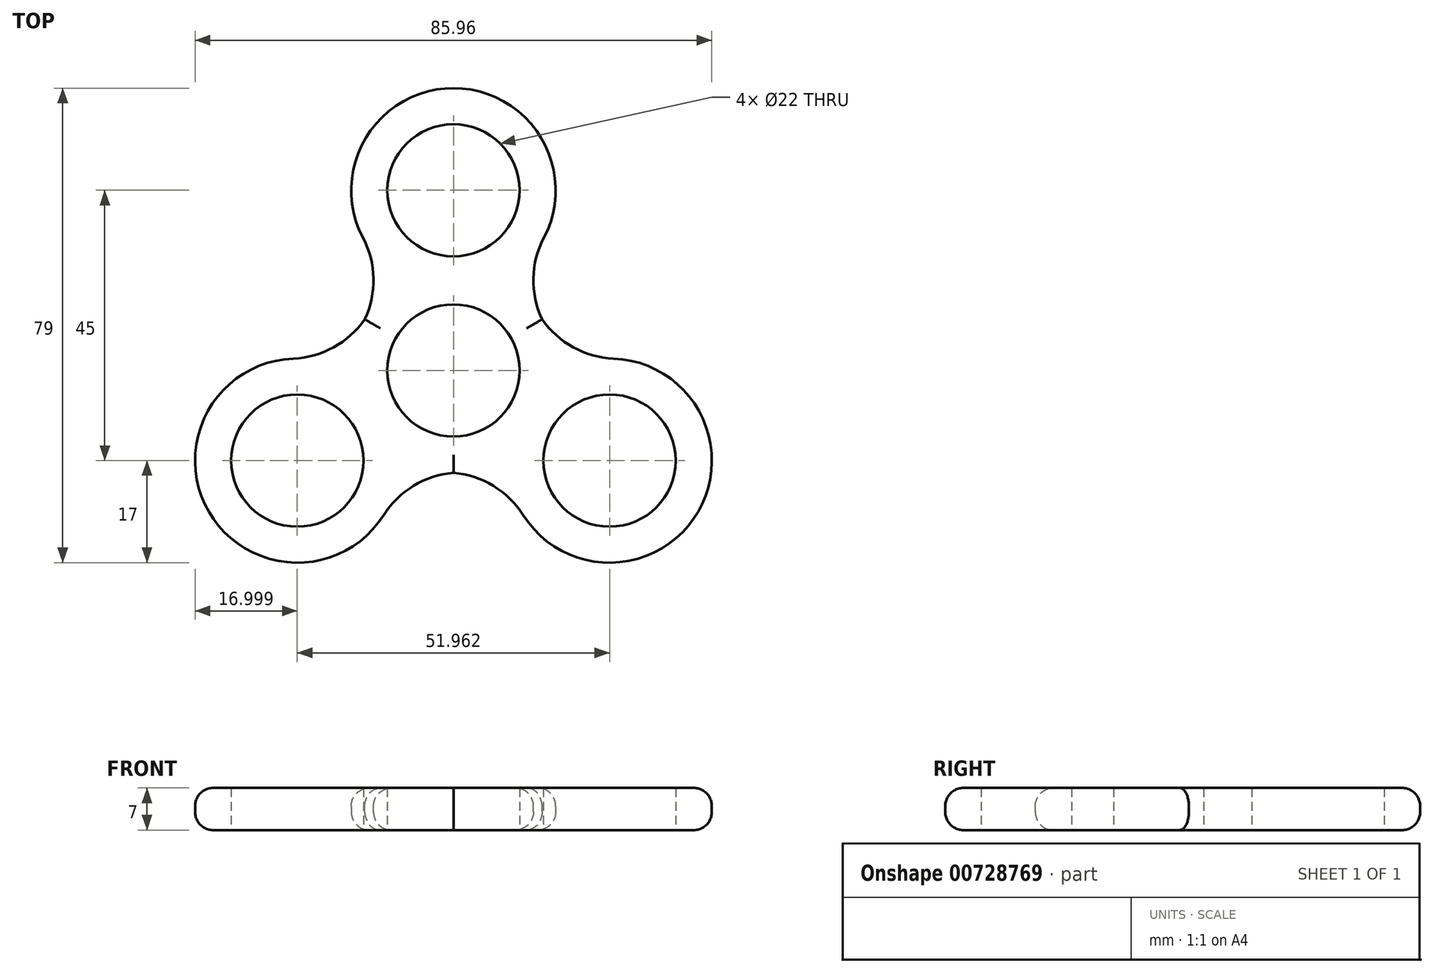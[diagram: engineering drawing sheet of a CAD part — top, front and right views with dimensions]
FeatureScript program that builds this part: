
annotation { "Feature Type Name" : "Feature", "Feature Type Description" : "" }
export const myFeature = defineFeature(function(context is Context, id is Id, definition is map)
    precondition{}
    {
        {
            var Q0;
            Q0=qCreatedBy(makeId("Top.planeOp"),FACE);
            var sketch = newSketch(context, id + "F0", { "sketchPlane" : qUnion([Q0])});
            skCircle(sketch, "E0", {"center": v(0, 0) * mm, "radius": 11 * mm});
            skCircle(sketch, "E1.0", {"center": v(0, 0) * mm, "radius": 17 * mm});
            skLineSegment(sketch, "E2", {"start": v(-11, 0) * mm, "end": v(0, 0) * mm});
            skLineSegment(sketch, "E3", {"start": v(0, 0) * mm, "end": v(0, 30) * mm});
            skCircle(sketch, "E4", {"center": v(0, 30) * mm, "radius": 11 * mm});
            skCircle(sketch, "E5.0", {"center": v(0, 30) * mm, "radius": 17 * mm});
            skCircle(sketch, "E6.1.1", {"center": v(-25.98, -15) * mm, "radius": 11 * mm});
            skCircle(sketch, "E6.1.2", {"center": v(-25.98, -15) * mm, "radius": 17 * mm});
            skCircle(sketch, "E6.2.1", {"center": v(25.98, -15) * mm, "radius": 11 * mm});
            skCircle(sketch, "E6.2.2", {"center": v(25.98, -15) * mm, "radius": 17 * mm});
            skLineSegment(sketch, "E7", {"start": v(-25.98, -15) * mm, "end": v(-25.98, 2) * mm});
            skLineSegment(sketch, "E8", {"start": v(0, 0) * mm, "end": v(0, -17) * mm});
            skSolve(sketch);
        }
        {
            var Q0;
            Q0=makeQuery(id+"F0.imprint","IMPRINT",FACE,{"disambiguationData":[TD([[makeQuery(id+"F0.imprint","IMPRINT",EDGE,{"derivedFrom":sQuery(id+"F0.wireOp",EDGE,"E4")}),-1.0]])]});
            var Q1;
            {var subQ0=sQuery(id+"F0.wireOp",EDGE,"E5.0");var subQ1=sQuery(id+"F0.wireOp",EDGE,"E1.0");var subQ2=makeQuery(id+"F0.imprint","INTERSECT",VERTEX,{"disambiguationData":[OD(1.0)],"derivedFrom":[subQ1,subQ0]});Q1=makeQuery(id+"F0.imprint","IMPRINT",FACE,{"disambiguationData":[TD([[makeQuery(id+"F0.imprint","IMPRINT",EDGE,{"disambiguationData":[TD([[subQ2,-1.0]])],"derivedFrom":subQ1}),1.0]])]});}
            var Q2;
            {var subQ1=sQuery(id+"F0.wireOp",EDGE,"E1.0");var subQ9=sQuery(id+"F0.wireOp",EDGE,"E8");var subQ10=makeQuery(id+"F0.imprint","INTERSECT",VERTEX,{"derivedFrom":[subQ1,subQ9]});Q2=makeQuery(id+"F0.imprint","IMPRINT",FACE,{"disambiguationData":[TD([[makeQuery(id+"F0.imprint","IMPRINT",EDGE,{"disambiguationData":[TD([[subQ10,-1.0]])],"derivedFrom":subQ1}),1.0]])]});}
            var Q3;
            {var subQ0=sQuery(id+"F0.wireOp",EDGE,"E6.2.2");var subQ1=sQuery(id+"F0.wireOp",EDGE,"E1.0");var subQ2=makeQuery(id+"F0.imprint","INTERSECT",VERTEX,{"disambiguationData":[OD(0.0)],"derivedFrom":[subQ1,subQ0]});Q3=makeQuery(id+"F0.imprint","IMPRINT",FACE,{"disambiguationData":[TD([[makeQuery(id+"F0.imprint","IMPRINT",EDGE,{"disambiguationData":[TD([[subQ2,-1.0]])],"derivedFrom":subQ1}),1.0]])]});}
            var Q4;
            {var subQ0=sQuery(id+"F0.wireOp",EDGE,"E6.1.2");var subQ1=sQuery(id+"F0.wireOp",EDGE,"E1.0");var subQ2=makeQuery(id+"F0.imprint","INTERSECT",VERTEX,{"disambiguationData":[OD(0.0)],"derivedFrom":[subQ1,subQ0]});Q4=makeQuery(id+"F0.imprint","IMPRINT",FACE,{"disambiguationData":[TD([[makeQuery(id+"F0.imprint","IMPRINT",EDGE,{"disambiguationData":[TD([[subQ2,-1.0]])],"derivedFrom":subQ1}),1.0]])]});}
            var Q5;
            Q5=makeQuery(id+"F0.imprint","IMPRINT",FACE,{"disambiguationData":[TD([[makeQuery(id+"F0.imprint","IMPRINT",EDGE,{"derivedFrom":sQuery(id+"F0.wireOp",EDGE,"E6.1.1")}),-1.0]])]});
            var Q6;
            {var subQ0=sQuery(id+"F0.wireOp",EDGE,"E3");var subQ1=sQuery(id+"F0.wireOp",EDGE,"E1.0");var subQ2=makeQuery(id+"F0.imprint","INTERSECT",VERTEX,{"derivedFrom":[subQ1,subQ0]});Q6=makeQuery(id+"F0.imprint","IMPRINT",FACE,{"disambiguationData":[TD([[makeQuery(id+"F0.imprint","IMPRINT",EDGE,{"disambiguationData":[TD([[subQ2,-1.0]])],"derivedFrom":subQ1}),1.0]])]});}
            var Q7;
            {var subQ0=sQuery(id+"F0.wireOp",EDGE,"E3");var subQ1=sQuery(id+"F0.wireOp",EDGE,"E1.0");var subQ2=makeQuery(id+"F0.imprint","INTERSECT",VERTEX,{"derivedFrom":[subQ1,subQ0]});Q7=makeQuery(id+"F0.imprint","IMPRINT",FACE,{"disambiguationData":[TD([[makeQuery(id+"F0.imprint","IMPRINT",EDGE,{"disambiguationData":[TD([[subQ2,1.0]])],"derivedFrom":subQ1}),1.0]])]});}
            var Q8;
            Q8=makeQuery(id+"F0.imprint","IMPRINT",FACE,{"disambiguationData":[TD([[makeQuery(id+"F0.imprint","IMPRINT",EDGE,{"derivedFrom":sQuery(id+"F0.wireOp",EDGE,"E6.2.1")}),-1.0]])]});
            extrude(context, id + "F1", {"entities" : qUnion([Q0, Q1, Q2, Q3, Q4, Q5, Q6, Q7, Q8]), "depth" : 7 * mm, "offsetDistance" : 25.4 * mm});
        }
        {
            var Q0;
            {var subQ0=sQuery(id+"F0.wireOp",EDGE,"E6.1.2");var subQ1=sQuery(id+"F0.wireOp",EDGE,"E1.0");Q0=makeQuery(id+"F1.opExtrude","SWEPT_EDGE",EDGE,{"disambiguationData":[OSD([subQ1,subQ0]),TDD([makeQuery(id+"F0.imprint","INTERSECT",VERTEX,{"disambiguationData":[OD(0.0)],"derivedFrom":[subQ1,subQ0]})])]});}
            var Q1;
            {var subQ0=sQuery(id+"F0.wireOp",EDGE,"E5.0");var subQ1=sQuery(id+"F0.wireOp",EDGE,"E1.0");Q1=makeQuery(id+"F1.opExtrude","SWEPT_EDGE",EDGE,{"disambiguationData":[OSD([subQ1,subQ0]),TDD([makeQuery(id+"F0.imprint","INTERSECT",VERTEX,{"disambiguationData":[OD(1.0)],"derivedFrom":[subQ1,subQ0]})])]});}
            var Q2;
            {var subQ0=sQuery(id+"F0.wireOp",EDGE,"E6.2.2");var subQ1=sQuery(id+"F0.wireOp",EDGE,"E1.0");Q2=makeQuery(id+"F1.opExtrude","SWEPT_EDGE",EDGE,{"disambiguationData":[OSD([subQ1,subQ0]),TDD([makeQuery(id+"F0.imprint","INTERSECT",VERTEX,{"disambiguationData":[OD(0.0)],"derivedFrom":[subQ1,subQ0]})])]});}
            var Q3;
            {var subQ0=sQuery(id+"F0.wireOp",EDGE,"E6.1.2");var subQ1=sQuery(id+"F0.wireOp",EDGE,"E1.0");Q3=makeQuery(id+"F1.opExtrude","SWEPT_EDGE",EDGE,{"disambiguationData":[OSD([subQ1,subQ0]),TDD([makeQuery(id+"F0.imprint","INTERSECT",VERTEX,{"disambiguationData":[OD(1.0)],"derivedFrom":[subQ1,subQ0]})])]});}
            var Q4;
            {var subQ0=sQuery(id+"F0.wireOp",EDGE,"E5.0");var subQ1=sQuery(id+"F0.wireOp",EDGE,"E1.0");Q4=makeQuery(id+"F1.opExtrude","SWEPT_EDGE",EDGE,{"disambiguationData":[OSD([subQ1,subQ0]),TDD([makeQuery(id+"F0.imprint","INTERSECT",VERTEX,{"disambiguationData":[OD(0.0)],"derivedFrom":[subQ1,subQ0]})])]});}
            var Q5;
            {var subQ0=sQuery(id+"F0.wireOp",EDGE,"E6.2.2");var subQ1=sQuery(id+"F0.wireOp",EDGE,"E1.0");Q5=makeQuery(id+"F1.opExtrude","SWEPT_EDGE",EDGE,{"disambiguationData":[OSD([subQ1,subQ0]),TDD([makeQuery(id+"F0.imprint","INTERSECT",VERTEX,{"disambiguationData":[OD(1.0)],"derivedFrom":[subQ1,subQ0]})])]});}
            fillet(context, id + "F2", {"entities" : qUnion([Q0, Q1, Q2, Q3, Q4, Q5]), "radius" : 15.24 * mm, "allowEdgeOverflow" : false});
        }
        {
            var Q0;
            Q0=makeQuery(id+"F1.opExtrude","CAP_EDGE",EDGE,{"disambiguationData":[OSD([sQuery(id+"F0.wireOp",EDGE,"E5.0")])],"isStart":false});
            var Q1;
            {var subQ0=sQuery(id+"F0.wireOp",EDGE,"E6.1.2");var subQ1=sQuery(id+"F0.wireOp",EDGE,"E1.0");Q1=makeQuery(id+"F2.opFillet","BLEND_EDGE",EDGE,{"blendedFrom":[makeQuery(id+"F1.opExtrude","SWEPT_EDGE",EDGE,{"disambiguationData":[OSD([subQ1,subQ0]),TDD([makeQuery(id+"F0.imprint","INTERSECT",VERTEX,{"disambiguationData":[OD(0.0)],"derivedFrom":[subQ1,subQ0]})])]}),makeQuery(id+"F1.opExtrude","CAP_FACE",FACE,{"disambiguationData":[OSD([subQ1,sQuery(id+"F0.wireOp",EDGE,"E4"),sQuery(id+"F0.wireOp",EDGE,"E5.0"),sQuery(id+"F0.wireOp",EDGE,"E6.1.1"),subQ0,sQuery(id+"F0.wireOp",EDGE,"E0"),sQuery(id+"F0.wireOp",EDGE,"E6.2.1"),sQuery(id+"F0.wireOp",EDGE,"E6.2.2")])],"isStart":false})],"blendedInto":[makeQuery(id+"F1.opExtrude","CAP_FACE",FACE,{"disambiguationData":[OSD([subQ1,sQuery(id+"F0.wireOp",EDGE,"E4"),sQuery(id+"F0.wireOp",EDGE,"E5.0"),sQuery(id+"F0.wireOp",EDGE,"E6.1.1"),subQ0,sQuery(id+"F0.wireOp",EDGE,"E0"),sQuery(id+"F0.wireOp",EDGE,"E6.2.1"),sQuery(id+"F0.wireOp",EDGE,"E6.2.2")])],"isStart":false})]});}
            var Q2;
            Q2=makeQuery(id+"F1.opExtrude","CAP_EDGE",EDGE,{"disambiguationData":[OSD([sQuery(id+"F0.wireOp",EDGE,"E6.1.2")])],"isStart":false});
            var Q3;
            Q3=makeQuery(id+"F1.opExtrude","CAP_EDGE",EDGE,{"disambiguationData":[OSD([sQuery(id+"F0.wireOp",EDGE,"E6.2.2")])],"isStart":false});
            var Q4;
            {var subQ0=sQuery(id+"F0.wireOp",EDGE,"E6.2.2");var subQ1=sQuery(id+"F0.wireOp",EDGE,"E1.0");Q4=makeQuery(id+"F2.opFillet","BLEND_EDGE",EDGE,{"blendedFrom":[makeQuery(id+"F1.opExtrude","SWEPT_EDGE",EDGE,{"disambiguationData":[OSD([subQ1,subQ0]),TDD([makeQuery(id+"F0.imprint","INTERSECT",VERTEX,{"disambiguationData":[OD(0.0)],"derivedFrom":[subQ1,subQ0]})])]}),makeQuery(id+"F1.opExtrude","CAP_FACE",FACE,{"disambiguationData":[OSD([subQ1,sQuery(id+"F0.wireOp",EDGE,"E4"),sQuery(id+"F0.wireOp",EDGE,"E5.0"),sQuery(id+"F0.wireOp",EDGE,"E6.1.1"),sQuery(id+"F0.wireOp",EDGE,"E6.1.2"),sQuery(id+"F0.wireOp",EDGE,"E0"),sQuery(id+"F0.wireOp",EDGE,"E6.2.1"),subQ0])],"isStart":false})],"blendedInto":[makeQuery(id+"F1.opExtrude","CAP_FACE",FACE,{"disambiguationData":[OSD([subQ1,sQuery(id+"F0.wireOp",EDGE,"E4"),sQuery(id+"F0.wireOp",EDGE,"E5.0"),sQuery(id+"F0.wireOp",EDGE,"E6.1.1"),sQuery(id+"F0.wireOp",EDGE,"E6.1.2"),sQuery(id+"F0.wireOp",EDGE,"E0"),sQuery(id+"F0.wireOp",EDGE,"E6.2.1"),subQ0])],"isStart":false})]});}
            var Q5;
            Q5=makeQuery(id+"F1.opExtrude","CAP_EDGE",EDGE,{"disambiguationData":[OSD([sQuery(id+"F0.wireOp",EDGE,"E5.0")])],"isStart":true});
            var Q6;
            {var subQ0=sQuery(id+"F0.wireOp",EDGE,"E5.0");var subQ1=sQuery(id+"F0.wireOp",EDGE,"E1.0");Q6=makeQuery(id+"F2.opFillet","BLEND_EDGE",EDGE,{"blendedFrom":[makeQuery(id+"F1.opExtrude","SWEPT_EDGE",EDGE,{"disambiguationData":[OSD([subQ1,subQ0]),TDD([makeQuery(id+"F0.imprint","INTERSECT",VERTEX,{"disambiguationData":[OD(1.0)],"derivedFrom":[subQ1,subQ0]})])]}),makeQuery(id+"F1.opExtrude","CAP_FACE",FACE,{"disambiguationData":[OSD([subQ1,sQuery(id+"F0.wireOp",EDGE,"E4"),subQ0,sQuery(id+"F0.wireOp",EDGE,"E6.1.1"),sQuery(id+"F0.wireOp",EDGE,"E6.1.2"),sQuery(id+"F0.wireOp",EDGE,"E0"),sQuery(id+"F0.wireOp",EDGE,"E6.2.1"),sQuery(id+"F0.wireOp",EDGE,"E6.2.2")])],"isStart":true})],"blendedInto":[makeQuery(id+"F1.opExtrude","CAP_FACE",FACE,{"disambiguationData":[OSD([subQ1,sQuery(id+"F0.wireOp",EDGE,"E4"),subQ0,sQuery(id+"F0.wireOp",EDGE,"E6.1.1"),sQuery(id+"F0.wireOp",EDGE,"E6.1.2"),sQuery(id+"F0.wireOp",EDGE,"E0"),sQuery(id+"F0.wireOp",EDGE,"E6.2.1"),sQuery(id+"F0.wireOp",EDGE,"E6.2.2")])],"isStart":true})]});}
            var Q7;
            {var subQ0=sQuery(id+"F0.wireOp",EDGE,"E6.1.2");var subQ1=sQuery(id+"F0.wireOp",EDGE,"E1.0");Q7=makeQuery(id+"F2.opFillet","BLEND_EDGE",EDGE,{"blendedFrom":[makeQuery(id+"F1.opExtrude","SWEPT_EDGE",EDGE,{"disambiguationData":[OSD([subQ1,subQ0]),TDD([makeQuery(id+"F0.imprint","INTERSECT",VERTEX,{"disambiguationData":[OD(0.0)],"derivedFrom":[subQ1,subQ0]})])]}),makeQuery(id+"F1.opExtrude","CAP_FACE",FACE,{"disambiguationData":[OSD([subQ1,sQuery(id+"F0.wireOp",EDGE,"E4"),sQuery(id+"F0.wireOp",EDGE,"E5.0"),sQuery(id+"F0.wireOp",EDGE,"E6.1.1"),subQ0,sQuery(id+"F0.wireOp",EDGE,"E0"),sQuery(id+"F0.wireOp",EDGE,"E6.2.1"),sQuery(id+"F0.wireOp",EDGE,"E6.2.2")])],"isStart":true})],"blendedInto":[makeQuery(id+"F1.opExtrude","CAP_FACE",FACE,{"disambiguationData":[OSD([subQ1,sQuery(id+"F0.wireOp",EDGE,"E4"),sQuery(id+"F0.wireOp",EDGE,"E5.0"),sQuery(id+"F0.wireOp",EDGE,"E6.1.1"),subQ0,sQuery(id+"F0.wireOp",EDGE,"E0"),sQuery(id+"F0.wireOp",EDGE,"E6.2.1"),sQuery(id+"F0.wireOp",EDGE,"E6.2.2")])],"isStart":true})]});}
            var Q8;
            Q8=makeQuery(id+"F1.opExtrude","CAP_EDGE",EDGE,{"disambiguationData":[OSD([sQuery(id+"F0.wireOp",EDGE,"E6.1.2")])],"isStart":true});
            var Q9;
            {var subQ0=sQuery(id+"F0.wireOp",EDGE,"E6.2.2");var subQ1=sQuery(id+"F0.wireOp",EDGE,"E1.0");Q9=makeQuery(id+"F2.opFillet","BLEND_EDGE",EDGE,{"blendedFrom":[makeQuery(id+"F1.opExtrude","SWEPT_EDGE",EDGE,{"disambiguationData":[OSD([subQ1,subQ0]),TDD([makeQuery(id+"F0.imprint","INTERSECT",VERTEX,{"disambiguationData":[OD(1.0)],"derivedFrom":[subQ1,subQ0]})])]}),makeQuery(id+"F1.opExtrude","CAP_FACE",FACE,{"disambiguationData":[OSD([subQ1,sQuery(id+"F0.wireOp",EDGE,"E4"),sQuery(id+"F0.wireOp",EDGE,"E5.0"),sQuery(id+"F0.wireOp",EDGE,"E6.1.1"),sQuery(id+"F0.wireOp",EDGE,"E6.1.2"),sQuery(id+"F0.wireOp",EDGE,"E0"),sQuery(id+"F0.wireOp",EDGE,"E6.2.1"),subQ0])],"isStart":true})],"blendedInto":[makeQuery(id+"F1.opExtrude","CAP_FACE",FACE,{"disambiguationData":[OSD([subQ1,sQuery(id+"F0.wireOp",EDGE,"E4"),sQuery(id+"F0.wireOp",EDGE,"E5.0"),sQuery(id+"F0.wireOp",EDGE,"E6.1.1"),sQuery(id+"F0.wireOp",EDGE,"E6.1.2"),sQuery(id+"F0.wireOp",EDGE,"E0"),sQuery(id+"F0.wireOp",EDGE,"E6.2.1"),subQ0])],"isStart":true})]});}
            var Q10;
            Q10=makeQuery(id+"F1.opExtrude","CAP_EDGE",EDGE,{"disambiguationData":[OSD([sQuery(id+"F0.wireOp",EDGE,"E6.2.2")])],"isStart":true});
            var Q11;
            {var subQ0=sQuery(id+"F0.wireOp",EDGE,"E5.0");var subQ1=sQuery(id+"F0.wireOp",EDGE,"E1.0");Q11=makeQuery(id+"F2.opFillet","BLEND_EDGE",EDGE,{"blendedFrom":[makeQuery(id+"F1.opExtrude","SWEPT_EDGE",EDGE,{"disambiguationData":[OSD([subQ1,subQ0]),TDD([makeQuery(id+"F0.imprint","INTERSECT",VERTEX,{"disambiguationData":[OD(0.0)],"derivedFrom":[subQ1,subQ0]})])]}),makeQuery(id+"F1.opExtrude","CAP_FACE",FACE,{"disambiguationData":[OSD([subQ1,sQuery(id+"F0.wireOp",EDGE,"E4"),subQ0,sQuery(id+"F0.wireOp",EDGE,"E6.1.1"),sQuery(id+"F0.wireOp",EDGE,"E6.1.2"),sQuery(id+"F0.wireOp",EDGE,"E0"),sQuery(id+"F0.wireOp",EDGE,"E6.2.1"),sQuery(id+"F0.wireOp",EDGE,"E6.2.2")])],"isStart":true})],"blendedInto":[makeQuery(id+"F1.opExtrude","CAP_FACE",FACE,{"disambiguationData":[OSD([subQ1,sQuery(id+"F0.wireOp",EDGE,"E4"),subQ0,sQuery(id+"F0.wireOp",EDGE,"E6.1.1"),sQuery(id+"F0.wireOp",EDGE,"E6.1.2"),sQuery(id+"F0.wireOp",EDGE,"E0"),sQuery(id+"F0.wireOp",EDGE,"E6.2.1"),sQuery(id+"F0.wireOp",EDGE,"E6.2.2")])],"isStart":true})]});}
            var Q12;
            {var subQ0=sQuery(id+"F0.wireOp",EDGE,"E6.2.2");var subQ1=sQuery(id+"F0.wireOp",EDGE,"E1.0");Q12=makeQuery(id+"F2.opFillet","BLEND_EDGE",EDGE,{"blendedFrom":[makeQuery(id+"F1.opExtrude","SWEPT_EDGE",EDGE,{"disambiguationData":[OSD([subQ1,subQ0]),TDD([makeQuery(id+"F0.imprint","INTERSECT",VERTEX,{"disambiguationData":[OD(0.0)],"derivedFrom":[subQ1,subQ0]})])]}),makeQuery(id+"F1.opExtrude","CAP_FACE",FACE,{"disambiguationData":[OSD([subQ1,sQuery(id+"F0.wireOp",EDGE,"E4"),sQuery(id+"F0.wireOp",EDGE,"E5.0"),sQuery(id+"F0.wireOp",EDGE,"E6.1.1"),sQuery(id+"F0.wireOp",EDGE,"E6.1.2"),sQuery(id+"F0.wireOp",EDGE,"E0"),sQuery(id+"F0.wireOp",EDGE,"E6.2.1"),subQ0])],"isStart":true})],"blendedInto":[makeQuery(id+"F1.opExtrude","CAP_FACE",FACE,{"disambiguationData":[OSD([subQ1,sQuery(id+"F0.wireOp",EDGE,"E4"),sQuery(id+"F0.wireOp",EDGE,"E5.0"),sQuery(id+"F0.wireOp",EDGE,"E6.1.1"),sQuery(id+"F0.wireOp",EDGE,"E6.1.2"),sQuery(id+"F0.wireOp",EDGE,"E0"),sQuery(id+"F0.wireOp",EDGE,"E6.2.1"),subQ0])],"isStart":true})]});}
            var Q13;
            {var subQ0=sQuery(id+"F0.wireOp",EDGE,"E6.1.2");var subQ1=sQuery(id+"F0.wireOp",EDGE,"E1.0");Q13=makeQuery(id+"F2.opFillet","BLEND_EDGE",EDGE,{"blendedFrom":[makeQuery(id+"F1.opExtrude","SWEPT_EDGE",EDGE,{"disambiguationData":[OSD([subQ1,subQ0]),TDD([makeQuery(id+"F0.imprint","INTERSECT",VERTEX,{"disambiguationData":[OD(1.0)],"derivedFrom":[subQ1,subQ0]})])]}),makeQuery(id+"F1.opExtrude","CAP_FACE",FACE,{"disambiguationData":[OSD([subQ1,sQuery(id+"F0.wireOp",EDGE,"E4"),sQuery(id+"F0.wireOp",EDGE,"E5.0"),sQuery(id+"F0.wireOp",EDGE,"E6.1.1"),subQ0,sQuery(id+"F0.wireOp",EDGE,"E0"),sQuery(id+"F0.wireOp",EDGE,"E6.2.1"),sQuery(id+"F0.wireOp",EDGE,"E6.2.2")])],"isStart":false})],"blendedInto":[makeQuery(id+"F1.opExtrude","CAP_FACE",FACE,{"disambiguationData":[OSD([subQ1,sQuery(id+"F0.wireOp",EDGE,"E4"),sQuery(id+"F0.wireOp",EDGE,"E5.0"),sQuery(id+"F0.wireOp",EDGE,"E6.1.1"),subQ0,sQuery(id+"F0.wireOp",EDGE,"E0"),sQuery(id+"F0.wireOp",EDGE,"E6.2.1"),sQuery(id+"F0.wireOp",EDGE,"E6.2.2")])],"isStart":false})]});}
            var Q14;
            {var subQ0=sQuery(id+"F0.wireOp",EDGE,"E6.1.2");var subQ1=sQuery(id+"F0.wireOp",EDGE,"E1.0");Q14=makeQuery(id+"F2.opFillet","BLEND_EDGE",EDGE,{"blendedFrom":[makeQuery(id+"F1.opExtrude","SWEPT_EDGE",EDGE,{"disambiguationData":[OSD([subQ1,subQ0]),TDD([makeQuery(id+"F0.imprint","INTERSECT",VERTEX,{"disambiguationData":[OD(1.0)],"derivedFrom":[subQ1,subQ0]})])]}),makeQuery(id+"F1.opExtrude","CAP_FACE",FACE,{"disambiguationData":[OSD([subQ1,sQuery(id+"F0.wireOp",EDGE,"E4"),sQuery(id+"F0.wireOp",EDGE,"E5.0"),sQuery(id+"F0.wireOp",EDGE,"E6.1.1"),subQ0,sQuery(id+"F0.wireOp",EDGE,"E0"),sQuery(id+"F0.wireOp",EDGE,"E6.2.1"),sQuery(id+"F0.wireOp",EDGE,"E6.2.2")])],"isStart":true})],"blendedInto":[makeQuery(id+"F1.opExtrude","CAP_FACE",FACE,{"disambiguationData":[OSD([subQ1,sQuery(id+"F0.wireOp",EDGE,"E4"),sQuery(id+"F0.wireOp",EDGE,"E5.0"),sQuery(id+"F0.wireOp",EDGE,"E6.1.1"),subQ0,sQuery(id+"F0.wireOp",EDGE,"E0"),sQuery(id+"F0.wireOp",EDGE,"E6.2.1"),sQuery(id+"F0.wireOp",EDGE,"E6.2.2")])],"isStart":true})]});}
            var Q15;
            {var subQ0=sQuery(id+"F0.wireOp",EDGE,"E5.0");var subQ1=sQuery(id+"F0.wireOp",EDGE,"E1.0");Q15=makeQuery(id+"F2.opFillet","BLEND_EDGE",EDGE,{"blendedFrom":[makeQuery(id+"F1.opExtrude","SWEPT_EDGE",EDGE,{"disambiguationData":[OSD([subQ1,subQ0]),TDD([makeQuery(id+"F0.imprint","INTERSECT",VERTEX,{"disambiguationData":[OD(0.0)],"derivedFrom":[subQ1,subQ0]})])]}),makeQuery(id+"F1.opExtrude","CAP_FACE",FACE,{"disambiguationData":[OSD([subQ1,sQuery(id+"F0.wireOp",EDGE,"E4"),subQ0,sQuery(id+"F0.wireOp",EDGE,"E6.1.1"),sQuery(id+"F0.wireOp",EDGE,"E6.1.2"),sQuery(id+"F0.wireOp",EDGE,"E0"),sQuery(id+"F0.wireOp",EDGE,"E6.2.1"),sQuery(id+"F0.wireOp",EDGE,"E6.2.2")])],"isStart":false})],"blendedInto":[makeQuery(id+"F1.opExtrude","CAP_FACE",FACE,{"disambiguationData":[OSD([subQ1,sQuery(id+"F0.wireOp",EDGE,"E4"),subQ0,sQuery(id+"F0.wireOp",EDGE,"E6.1.1"),sQuery(id+"F0.wireOp",EDGE,"E6.1.2"),sQuery(id+"F0.wireOp",EDGE,"E0"),sQuery(id+"F0.wireOp",EDGE,"E6.2.1"),sQuery(id+"F0.wireOp",EDGE,"E6.2.2")])],"isStart":false})]});}
            var Q16;
            {var subQ0=sQuery(id+"F0.wireOp",EDGE,"E5.0");var subQ1=sQuery(id+"F0.wireOp",EDGE,"E1.0");Q16=makeQuery(id+"F2.opFillet","BLEND_EDGE",EDGE,{"blendedFrom":[makeQuery(id+"F1.opExtrude","SWEPT_EDGE",EDGE,{"disambiguationData":[OSD([subQ1,subQ0]),TDD([makeQuery(id+"F0.imprint","INTERSECT",VERTEX,{"disambiguationData":[OD(1.0)],"derivedFrom":[subQ1,subQ0]})])]}),makeQuery(id+"F1.opExtrude","CAP_FACE",FACE,{"disambiguationData":[OSD([subQ1,sQuery(id+"F0.wireOp",EDGE,"E4"),subQ0,sQuery(id+"F0.wireOp",EDGE,"E6.1.1"),sQuery(id+"F0.wireOp",EDGE,"E6.1.2"),sQuery(id+"F0.wireOp",EDGE,"E0"),sQuery(id+"F0.wireOp",EDGE,"E6.2.1"),sQuery(id+"F0.wireOp",EDGE,"E6.2.2")])],"isStart":false})],"blendedInto":[makeQuery(id+"F1.opExtrude","CAP_FACE",FACE,{"disambiguationData":[OSD([subQ1,sQuery(id+"F0.wireOp",EDGE,"E4"),subQ0,sQuery(id+"F0.wireOp",EDGE,"E6.1.1"),sQuery(id+"F0.wireOp",EDGE,"E6.1.2"),sQuery(id+"F0.wireOp",EDGE,"E0"),sQuery(id+"F0.wireOp",EDGE,"E6.2.1"),sQuery(id+"F0.wireOp",EDGE,"E6.2.2")])],"isStart":false})]});}
            fillet(context, id + "F3", {"entities" : qUnion([Q0, Q1, Q2, Q3, Q4, Q5, Q6, Q7, Q8, Q9, Q10, Q11, Q12, Q13, Q14, Q15, Q16]), "radius" : 3 * mm, "tangentPropagation" : true, "allowEdgeOverflow" : false});
        }
    });
